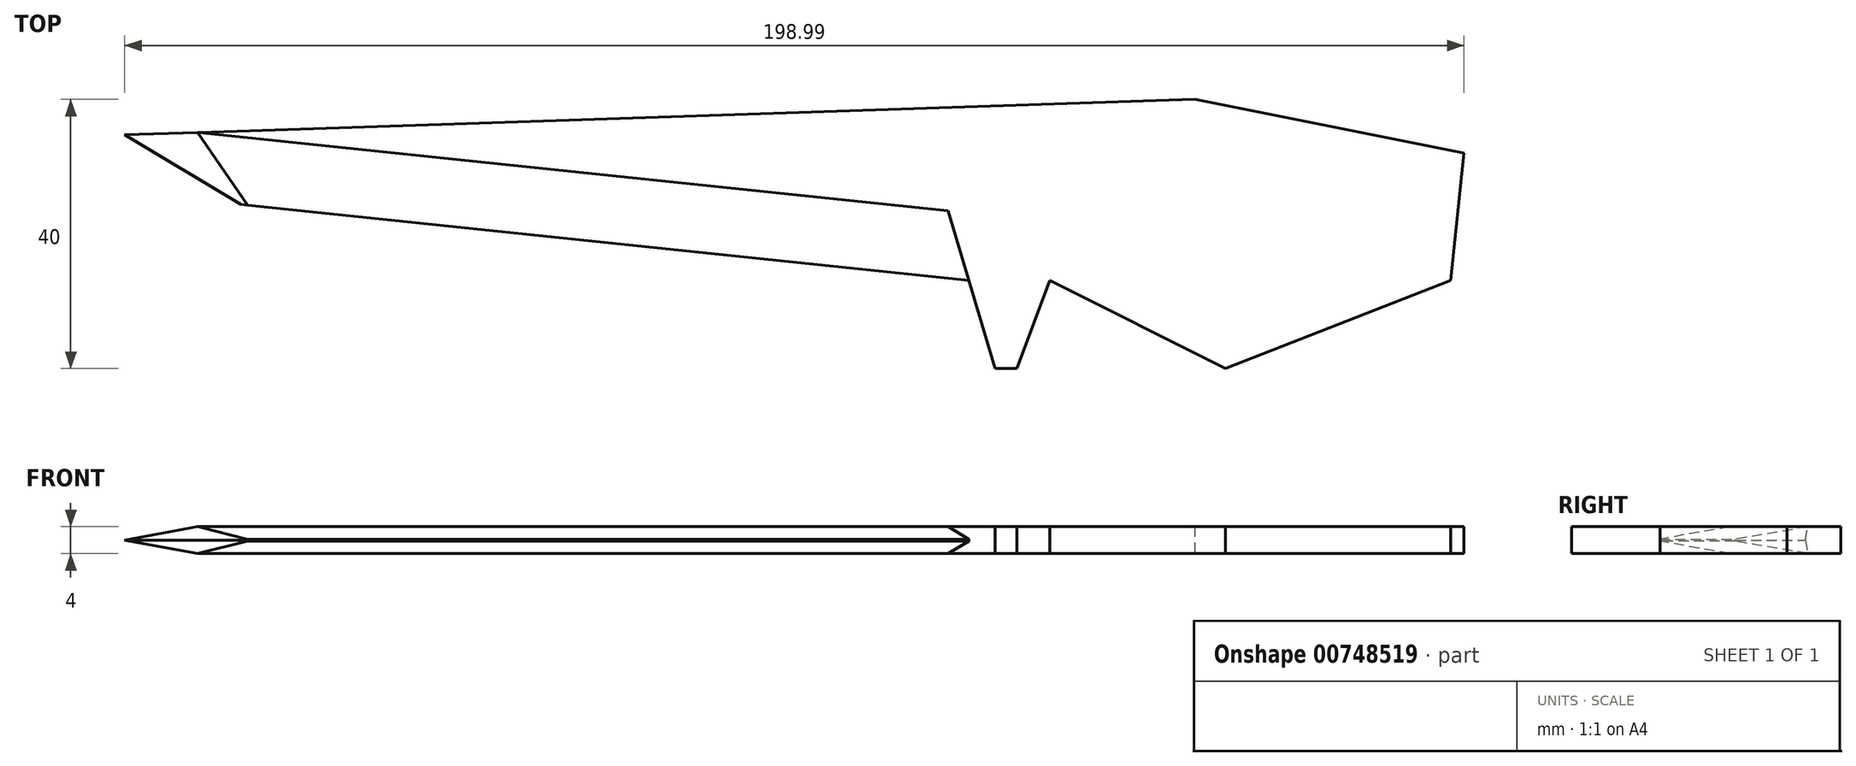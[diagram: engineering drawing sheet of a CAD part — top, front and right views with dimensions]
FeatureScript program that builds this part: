
annotation { "Feature Type Name" : "Feature", "Feature Type Description" : "" }
export const myFeature = defineFeature(function(context is Context, id is Id, definition is map)
    precondition{}
    {
        {
            var Q0;
            Q0=qCreatedBy(makeId("Top.planeOp"),FACE);
            var sketch = newSketch(context, id + "F0", { "sketchPlane" : qUnion([Q0])});
            skLineSegment(sketch, "E0", {"start": v(-72.1, 12.52) * mm, "end": v(48.03, 0) * mm});
            skLineSegment(sketch, "E1", {"start": v(48.03, 0) * mm, "end": v(51.9, -13.1) * mm});
            skLineSegment(sketch, "E2", {"start": v(51.9, -13.1) * mm, "end": v(55.17, -13.1) * mm});
            skLineSegment(sketch, "E3", {"start": v(55.17, -13.1) * mm, "end": v(60.06, 0) * mm});
            skLineSegment(sketch, "E4", {"start": v(60.06, 0) * mm, "end": v(86.17, -13.1) * mm});
            skLineSegment(sketch, "E5", {"start": v(86.17, -13.1) * mm, "end": v(119.62, 0) * mm});
            skLineSegment(sketch, "E6", {"start": v(119.62, 0) * mm, "end": v(121.59, 18.9) * mm});
            skLineSegment(sketch, "E7", {"start": v(121.59, 18.9) * mm, "end": v(81.59, 26.9) * mm});
            skLineSegment(sketch, "E8", {"start": v(81.59, 26.9) * mm, "end": v(-78.32, 21.59) * mm});
            skLineSegment(sketch, "E9", {"start": v(-78.32, 21.59) * mm, "end": v(-72.1, 12.52) * mm});
            skSolve(sketch);
        }
        {
            var Q0;
            Q0=makeQuery(id+"F0.imprint","IMPRINT",FACE,{"disambiguationData":[TD([[makeQuery(id+"F0.imprint","IMPRINT",EDGE,{"derivedFrom":sQuery(id+"F0.wireOp",EDGE,"E0")}),1.0]])]});
            extrude(context, id + "F1", {"entities" : qUnion([Q0]), "endBound" : BoundingType.SYMMETRIC, "depth" : 4 * mm, "offsetDistance" : 25 * mm});
        }
        {
            var Q0;
            Q0=makeQuery(id+"F1.opExtrude","CAP_EDGE",EDGE,{"disambiguationData":[OSD([sQuery(id+"F0.wireOp",EDGE,"E0")])],"isStart":false});
            var Q1;
            Q1=makeQuery(id+"F1.opExtrude","CAP_EDGE",EDGE,{"disambiguationData":[OSD([sQuery(id+"F0.wireOp",EDGE,"E0")])],"isStart":true});
            chamfer(context, id + "F2", {"entities" : qUnion([Q0, Q1]), "chamferType" : ChamferType.TWO_OFFSETS, "width1" : 10 * mm, "oppositeDirection" : false, "width2" : 1.85 * mm, "tangentPropagation" : true});
        }
        {
            var Q0;
            Q0=makeQuery(id+"F2.opChamfer","BLEND_EDGE",EDGE,{"blendedFrom":[makeQuery(id+"F1.opExtrude","CAP_EDGE",EDGE,{"disambiguationData":[OSD([sQuery(id+"F0.wireOp",EDGE,"E0")])],"isStart":true}),makeQuery(id+"F1.opExtrude","SWEPT_FACE",FACE,{"disambiguationData":[OSD([sQuery(id+"F0.wireOp",EDGE,"E9")])]})],"blendedInto":[makeQuery(id+"F1.opExtrude","SWEPT_FACE",FACE,{"disambiguationData":[OSD([sQuery(id+"F0.wireOp",EDGE,"E9")])]})]});
            var Q1;
            Q1=makeQuery(id+"F2.opChamfer","BLEND_EDGE",EDGE,{"blendedFrom":[makeQuery(id+"F1.opExtrude","CAP_EDGE",EDGE,{"disambiguationData":[OSD([sQuery(id+"F0.wireOp",EDGE,"E0")])],"isStart":false}),makeQuery(id+"F1.opExtrude","SWEPT_FACE",FACE,{"disambiguationData":[OSD([sQuery(id+"F0.wireOp",EDGE,"E9")])]})],"blendedInto":[makeQuery(id+"F1.opExtrude","SWEPT_FACE",FACE,{"disambiguationData":[OSD([sQuery(id+"F0.wireOp",EDGE,"E9")])]})]});
            chamfer(context, id + "F3", {"entities" : qUnion([Q0, Q1]), "chamferType" : ChamferType.TWO_OFFSETS, "width1" : 1.85 * mm, "oppositeDirection" : false, "width2" : 10 * mm, "tangentPropagation" : true});
        }
    });
